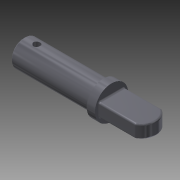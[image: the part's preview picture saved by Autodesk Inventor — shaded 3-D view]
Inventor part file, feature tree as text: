
AUTODESK INVENTOR PART (.ipt)
format: ipt  version: 2011 SP2 (Build 150309200, 309)  size: 153,088 bytes
history: native  units: mm
features: sketch x4, extrude x3, fillet x2, revolve x1, chamfer x1, projected_geometry x1
ambient origin geometry x8: Origin, YZ Plane, XZ Plane, XY Plane, X Axis, Y Axis, Z Axis, Center Point
bodies: Solid1 (feature_tree)
feature tree (12):
  revolve  "Revolution1"  [1 undecoded]
  extrude  "Extrusion1"  Depth=48.0mm
  extrude  "Extrusion2"  TaperAngle=90.0deg  [1 undecoded]
  fillet  "Fillet1"  Radius=8.0mm
  fillet  "Fillet2"  Radius=16.0mm
  chamfer  "Chamfer1"  Distance=27.0mm
  extrude  "Extrusion3"  Depth=27.0mm TaperAngle=0.0deg
  sketch  "Sketch1"  dims[d0=5.0mm d1=10.0mm]
  sketch  "Sketch2"  dims[d2=2.0mm d3=48.0mm]
  sketch  "Sketch3"  dims[d4=8.0mm d5=90.0deg d6=8.0mm d7=16.0mm d8=27.0mm d9=0.0mm]
  projected_geometry  "Projected Loop1"
  sketch  "Sketch4"  dims[d10=9.0mm d11=27.0mm d12=0.0mm d13=1.0mm d14=1.0mm d15=1.0mm d16=2.0mm d17=45.0deg d18=2.0mm d19=40.0mm d20=27.0mm d21=0.0mm]
note: 2 required parameter values undecoded (feature->parameter linkage not recoverable at this tier; creation-order binding heuristic only, values carry confidence <= 0.55)